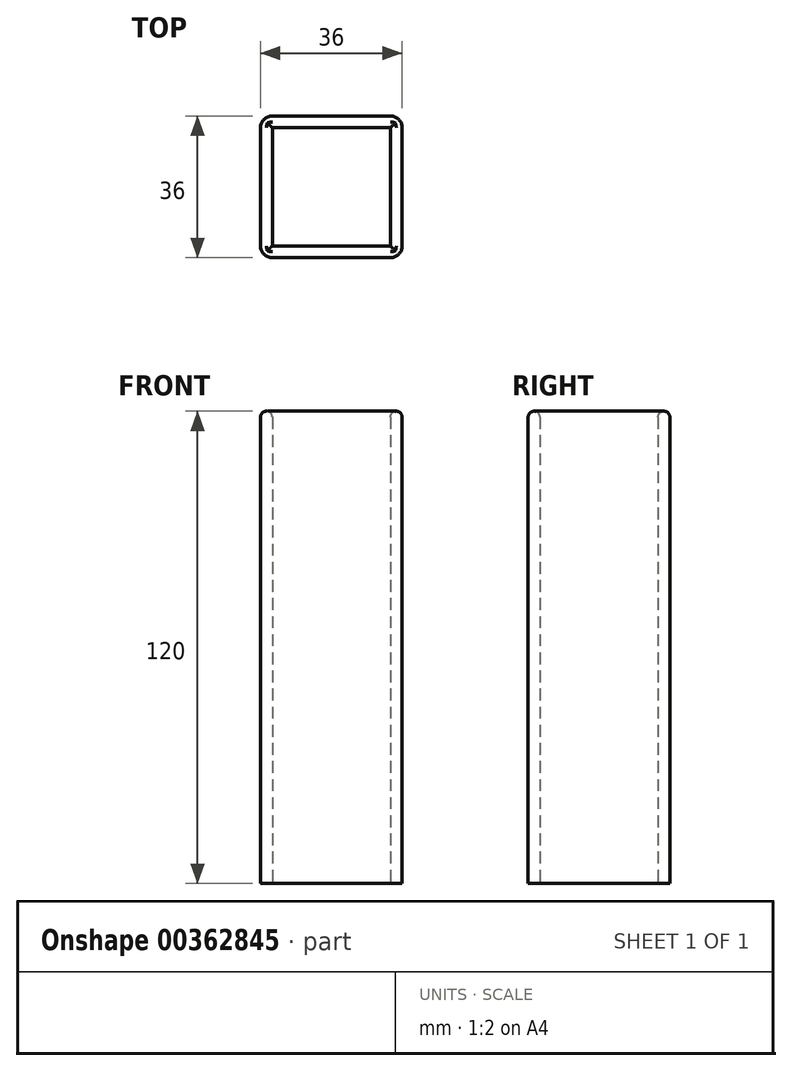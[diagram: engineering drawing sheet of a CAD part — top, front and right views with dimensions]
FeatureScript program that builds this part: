
annotation { "Feature Type Name" : "Feature", "Feature Type Description" : "" }
export const myFeature = defineFeature(function(context is Context, id is Id, definition is map)
    precondition{}
    {
        {
            var Q0;
            Q0=qCreatedBy(makeId("Top.planeOp"),FACE);
            var sketch = newSketch(context, id + "F0", { "sketchPlane" : qUnion([Q0])});
            skLineSegment(sketch, "E0.bottom", {"start": v(3, 0) * mm, "end": v(33, 0) * mm});
            skLineSegment(sketch, "E0.top", {"start": v(3, -36) * mm, "end": v(33, -36) * mm});
            skLineSegment(sketch, "E0.left", {"start": v(0, -3) * mm, "end": v(0, -33) * mm});
            skLineSegment(sketch, "E0.right", {"start": v(36, -3) * mm, "end": v(36, -33) * mm});
            skLineSegment(sketch, "E1.bottom", {"start": v(3, -3) * mm, "end": v(33, -3) * mm});
            skLineSegment(sketch, "E1.top", {"start": v(3, -33) * mm, "end": v(33, -33) * mm});
            skLineSegment(sketch, "E1.left", {"start": v(3, -3) * mm, "end": v(3, -33) * mm});
            skLineSegment(sketch, "E1.right", {"start": v(33, -3) * mm, "end": v(33, -33) * mm});
            skPoint(sketch, "E2.visualSharp", {"position": v(0, 0) * mm});
            skArc(sketch, "E2.filletArc", {"start": v(3, 0) * mm, "mid": v(0.88, -0.88) * mm, "end": v(0, -3) * mm});
            skPoint(sketch, "E3.visualSharp", {"position": v(0, -36) * mm});
            skArc(sketch, "E3.filletArc", {"start": v(0, -33) * mm, "mid": v(0.88, -35.12) * mm, "end": v(3, -36) * mm});
            skPoint(sketch, "E4.visualSharp", {"position": v(36, -36) * mm});
            skArc(sketch, "E4.filletArc", {"start": v(33, -36) * mm, "mid": v(35.12, -35.12) * mm, "end": v(36, -33) * mm});
            skPoint(sketch, "E5.visualSharp", {"position": v(36, 0) * mm});
            skArc(sketch, "E5.filletArc", {"start": v(36, -3) * mm, "mid": v(35.12, -0.88) * mm, "end": v(33, 0) * mm});
            skSolve(sketch);
        }
        {
            var Q0;
            Q0 = qSketchRegion(id + "F0", true);
            extrude(context, id + "F1", {"entities" : qUnion([Q0]), "depth" : 120 * mm});
        }
        {
            var Q0;
            Q0=makeQuery(id+"F1.opExtrude","CAP_EDGE",EDGE,{"disambiguationData":[OSD([sQuery(id+"F0.wireOp",EDGE,"E1.top")])],"isStart":false});
            var Q1;
            Q1=makeQuery(id+"F1.opExtrude","CAP_EDGE",EDGE,{"disambiguationData":[OSD([sQuery(id+"F0.wireOp",EDGE,"E1.left")])],"isStart":false});
            var Q2;
            Q2=makeQuery(id+"F1.opExtrude","CAP_EDGE",EDGE,{"disambiguationData":[OSD([sQuery(id+"F0.wireOp",EDGE,"E1.bottom")])],"isStart":false});
            var Q3;
            Q3=makeQuery(id+"F1.opExtrude","CAP_EDGE",EDGE,{"disambiguationData":[OSD([sQuery(id+"F0.wireOp",EDGE,"E1.right")])],"isStart":false});
            fillet(context, id + "F2", {"entities" : qUnion([Q0, Q1, Q2, Q3]), "radius" : 1.5 * mm, "tangentPropagation" : true, "allowEdgeOverflow" : false});
        }
        {
            var Q0;
            Q0=makeQuery(id+"F1.opExtrude","CAP_EDGE",EDGE,{"disambiguationData":[OSD([sQuery(id+"F0.wireOp",EDGE,"E0.right")])],"isStart":false});
            var Q1;
            Q1=makeQuery(id+"F1.opExtrude","CAP_EDGE",EDGE,{"disambiguationData":[OSD([sQuery(id+"F0.wireOp",EDGE,"E5.filletArc")])],"isStart":false});
            var Q2;
            Q2=makeQuery(id+"F1.opExtrude","CAP_EDGE",EDGE,{"disambiguationData":[OSD([sQuery(id+"F0.wireOp",EDGE,"E0.bottom")])],"isStart":false});
            var Q3;
            Q3=makeQuery(id+"F1.opExtrude","CAP_EDGE",EDGE,{"disambiguationData":[OSD([sQuery(id+"F0.wireOp",EDGE,"E2.filletArc")])],"isStart":false});
            fillet(context, id + "F3", {"entities" : qUnion([Q0, Q1, Q2, Q3]), "radius" : 1.5 * mm, "tangentPropagation" : true, "allowEdgeOverflow" : false});
        }
    });
